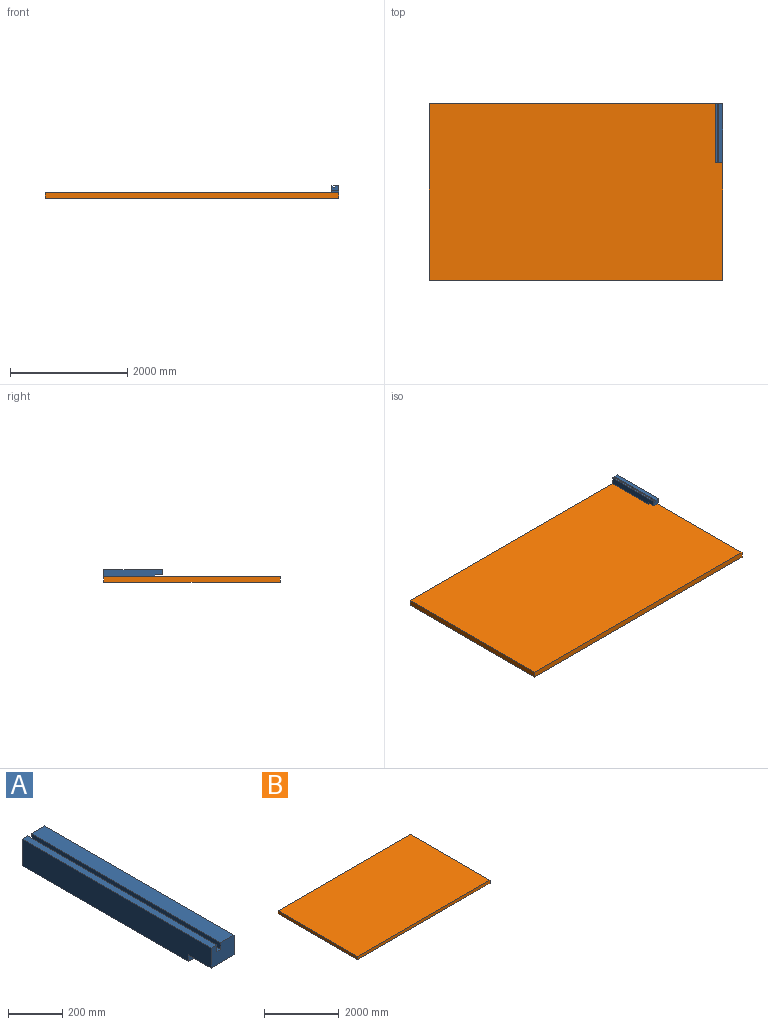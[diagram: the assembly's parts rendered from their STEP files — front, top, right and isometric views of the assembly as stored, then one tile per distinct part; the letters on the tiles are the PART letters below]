
ASSEMBLY  parts=2 mates=1
PART A: 12 faces, bbox 120x990x120 mm
  f0: plane 990x30mm, normal (0,0,1), area 29700mm2, adj f1,f2,f6,f9
  f1: plane 120x90mm, normal (0,-1,0), area 10200mm2, adj f0,f2,f4,f5,f7,f9,f10,f11
  f2: plane 990x120mm, normal (-1,0,0), area 115200mm2, adj f0,f1,f3,f6,f7,f8
  f3: plane 870x120mm, normal (0,0,-1), area 104400mm2, adj f2,f4,f6,f8
  f4: plane 990x120mm, normal (1,0,0), area 115200mm2, adj f1,f3,f5,f6,f7,f8
  f5: plane 990x70mm, normal (0,0,1), area 69300mm2, adj f1,f4,f6,f11
  f6: plane 120x120mm, normal (0,1,0), area 13800mm2, adj f0,f2,f3,f4,f5,f9,f10,f11
  f7: plane 120x120mm, normal (0,0,-1), area 14400mm2, adj f1,f2,f4,f8
  f8: plane 120x30mm, normal (0,-1,0), area 3600mm2, adj f2,f3,f4,f7
  f9: plane 990x30mm, normal (1,0,0), area 29700mm2, adj f0,f1,f6,f10
  f10: plane 990x20mm, normal (0,0,1), area 19800mm2, adj f1,f6,f9,f11
  f11: plane 990x30mm, normal (-1,0,0), area 29700mm2, adj f1,f5,f6,f10
PART B: 6 faces, bbox 5000x3000x100 mm
  f0: plane 3000x100mm, normal (-1,0,0), area 300000mm2, adj f1,f3,f4,f5
  f1: plane 5000x100mm, normal (0,-1,0), area 500000mm2, adj f0,f2,f4,f5
  f2: plane 3000x100mm, normal (1,0,0), area 300000mm2, adj f1,f3,f4,f5
  f3: plane 5000x100mm, normal (0,1,0), area 500000mm2, adj f0,f2,f4,f5
  f4: plane 5000x3000mm, normal (0,0,1), area 15000000mm2, adj f0,f1,f2,f3
  f5: plane 5000x3000mm, normal (0,0,-1), area 15000000mm2, adj f0,f1,f2,f3
PLACE A t=(2440.23,509.6,109.19)mm
PLACE B t=(0.23,-0.4,-50.81)mm fixed
MATE fastened A.f3 <-> B.f4  axis (0,0,1) through (2500.23,1499.6,49.19)mm
